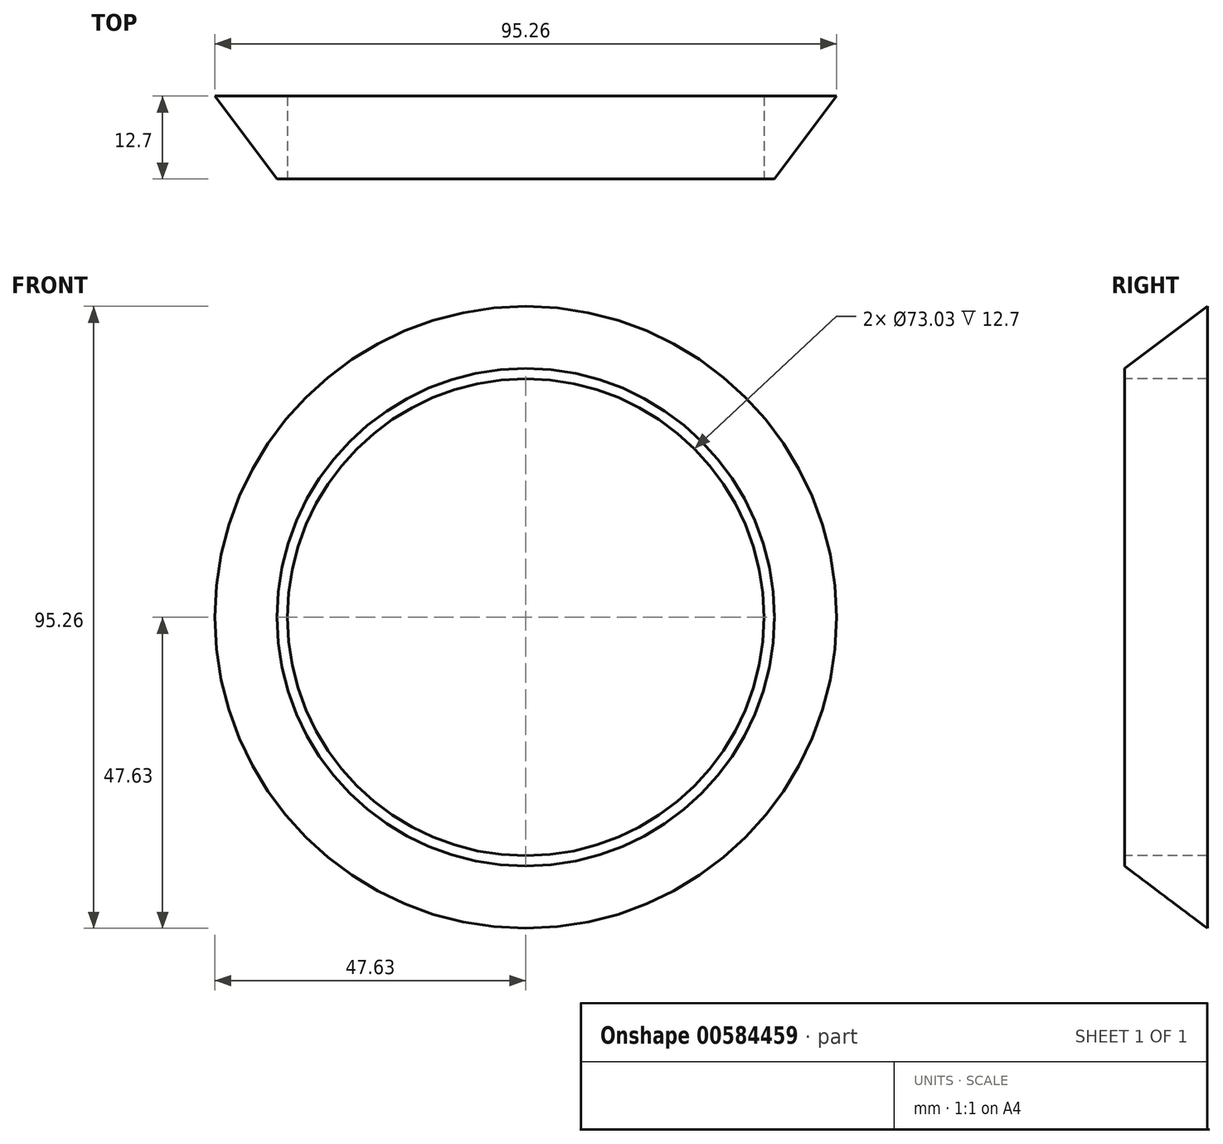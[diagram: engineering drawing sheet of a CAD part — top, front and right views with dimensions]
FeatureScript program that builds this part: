
annotation { "Feature Type Name" : "Feature", "Feature Type Description" : "" }
export const myFeature = defineFeature(function(context is Context, id is Id, definition is map)
    precondition{}
    {
        {
            var Q0;
            Q0=qCreatedBy(makeId("Front.planeOp"),FACE);
            var sketch = newSketch(context, id + "F0", { "sketchPlane" : qUnion([Q0])});
            skCircle(sketch, "E0", {"center": v(0, 0) * mm, "radius": 38.1 * mm});
            skSolve(sketch);
        }
        {
            var Q0;
            Q0=qCreatedBy(makeId("Front.planeOp"),FACE);
            cPlane(context, id + "F1", {"entities" : qUnion([Q0]), "cplaneType" : CPlaneType.OFFSET, "offset" : 12.7 * mm, "oppositeDirection" : true, "width" : 152.4 * mm, "height" : 152.4 * mm});
        }
        {
            var Q0;
            Q0=qCreatedBy(id+"F1.planeOp",FACE);
            var sketch = newSketch(context, id + "F2", { "sketchPlane" : qUnion([Q0])});
            skCircle(sketch, "E1", {"center": v(0, 0) * mm, "radius": 47.63 * mm});
            skSolve(sketch);
        }
        {
            var Q0;
            Q0=makeQuery(id+"F0.imprint","IMPRINT",FACE,{"disambiguationData":[TD([[makeQuery(id+"F0.imprint","IMPRINT",EDGE,{"derivedFrom":sQuery(id+"F0.wireOp",EDGE,"E0")}),1.0]])]});
            var Q1;
            Q1=makeQuery(id+"F2.imprint","IMPRINT",FACE,{"disambiguationData":[TD([[makeQuery(id+"F2.imprint","IMPRINT",EDGE,{"derivedFrom":sQuery(id+"F2.wireOp",EDGE,"E1")}),1.0]])]});
            loft(context, id + "F3", {"sheetProfilesArray" : [{ "sheetProfileEntities" : qUnion([Q0]) }, { "sheetProfileEntities" : qUnion([Q1]) }]});
        }
        {
            var Q0;
            Q0=qCreatedBy(makeId("Front.planeOp"),FACE);
            var sketch = newSketch(context, id + "F4", { "sketchPlane" : qUnion([Q0])});
            skCircle(sketch, "E2", {"center": v(0, 0) * mm, "radius": 36.51 * mm});
            skSolve(sketch);
        }
        {
            var Q0;
            Q0 = qSketchRegion(id + "F4", true);
            extrude(context, id + "F5", {"entities" : qUnion([Q0]), "operationType" : NewBodyOperationType.REMOVE, "oppositeDirection" : true, "depth" : 25.4 * mm, "offsetDistance" : 25.4 * mm});
        }
    });
